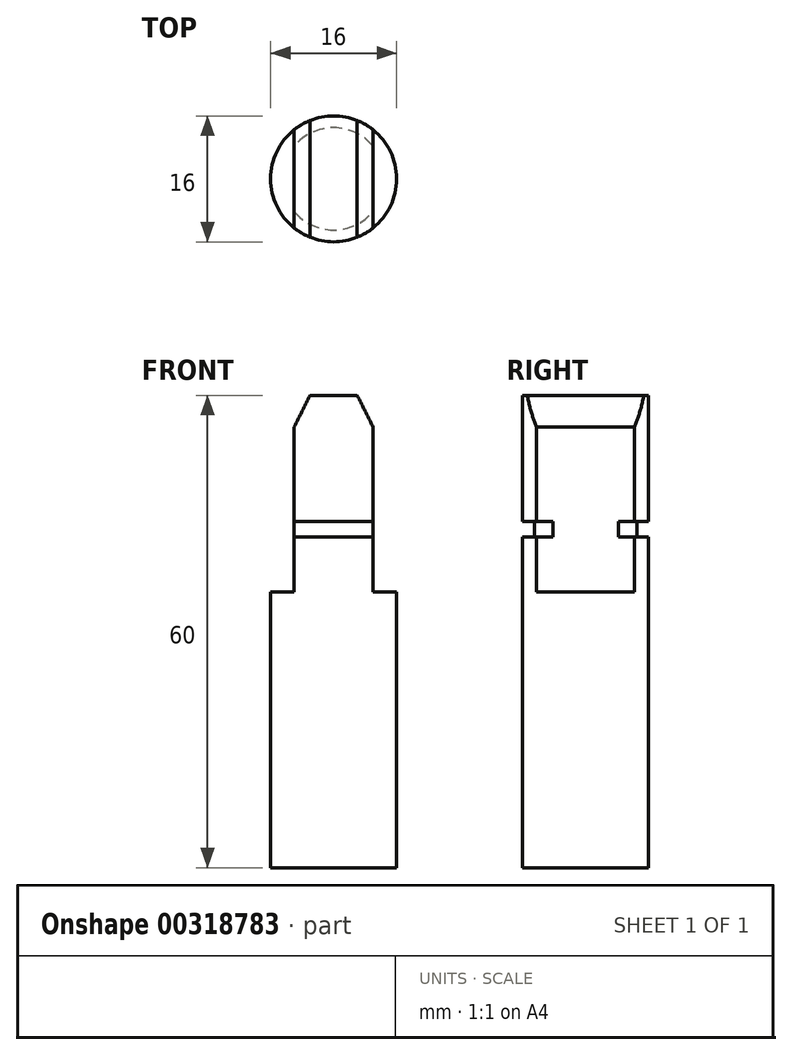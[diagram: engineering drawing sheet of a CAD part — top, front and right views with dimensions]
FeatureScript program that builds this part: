
annotation { "Feature Type Name" : "Feature", "Feature Type Description" : "" }
export const myFeature = defineFeature(function(context is Context, id is Id, definition is map)
    precondition{}
    {
        {
            var Q0;
            Q0=qCreatedBy(makeId("Top.planeOp"),FACE);
            var sketch = newSketch(context, id + "F0", { "sketchPlane" : qUnion([Q0])});
            skCircle(sketch, "E0", {"center": v(0, 0) * mm, "radius": 8 * mm});
            skSolve(sketch);
        }
        {
            var Q0;
            Q0=makeQuery(id+"F0.imprint","IMPRINT",FACE,{"disambiguationData":[TD([[makeQuery(id+"F0.imprint","IMPRINT",EDGE,{"derivedFrom":sQuery(id+"F0.wireOp",EDGE,"E0")}),1.0]])]});
            extrude(context, id + "F1", {"entities" : qUnion([Q0]), "depth" : 35 * mm, "symmetric" : true});
        }
        {
            var Q0;
            Q0=makeQuery(id+"F1.opExtrude","CAP_FACE",FACE,{"disambiguationData":[OSD([sQuery(id+"F0.wireOp",EDGE,"E0")])],"isStart":false});
            var sketch = newSketch(context, id + "F2", { "sketchPlane" : qUnion([Q0])});
            skLineSegment(sketch, "E1", {"start": v(-5, 6.24) * mm, "end": v(-5, -6.24) * mm});
            skLineSegment(sketch, "E2.MirrorCS", {"start": v(5, 6.24) * mm, "end": v(5, -6.24) * mm});
            skArc(sketch, "E3", {"start": v(5, 6.24) * mm, "mid": v(0, 11.24) * mm, "end": v(-5, 6.24) * mm});
            skArc(sketch, "E4.MirrorCS", {"start": v(5, -6.24) * mm, "mid": v(0, -11.24) * mm, "end": v(-5, -6.24) * mm});
            skSolve(sketch);
        }
        {
            var Q0;
            Q0=makeQuery(id+"F2.imprint","IMPRINT",FACE,{"disambiguationData":[TD([[makeQuery(id+"F2.imprint","IMPRINT",EDGE,{"derivedFrom":sQuery(id+"F2.wireOp",EDGE,"E1")}),1.0]])]});
            extrude(context, id + "F3", {"entities" : qUnion([Q0]), "operationType" : NewBodyOperationType.ADD, "depth" : 25 * mm});
        }
        {
            var Q0;
            Q0=makeQuery(id+"F3.opExtrude","CAP_EDGE",EDGE,{"disambiguationData":[OSD([sQuery(id+"F2.wireOp",EDGE,"E1")])],"isStart":false});
            var Q1;
            Q1=makeQuery(id+"F3.opExtrude","CAP_EDGE",EDGE,{"disambiguationData":[OSD([sQuery(id+"F2.wireOp",EDGE,"E2.MirrorCS")])],"isStart":false});
            chamfer(context, id + "F4", {"entities" : qUnion([Q0, Q1]), "chamferType" : ChamferType.TWO_OFFSETS, "width1" : 2 * mm, "oppositeDirection" : false, "width2" : 4 * mm, "tangentPropagation" : true});
        }
        {
            var Q0;
            Q0=qCreatedBy(makeId("Top.planeOp"),FACE);
            cPlane(context, id + "F5", {"entities" : qUnion([Q0]), "cplaneType" : CPlaneType.OFFSET, "offset" : 26.5 * mm, "width" : 150 * mm, "height" : 150 * mm});
        }
        {
            var Q0;
            Q0=qCreatedBy(id+"F5.planeOp",FACE);
            var sketch = newSketch(context, id + "F6", { "sketchPlane" : qUnion([Q0])});
            skCircle(sketch, "E5", {"center": v(0, 0) * mm, "radius": 8 * mm});
            skCircle(sketch, "E6", {"center": v(0, 0) * mm, "radius": 6.5 * mm});
            skSolve(sketch);
        }
        {
            var Q0;
            Q0=makeQuery(id+"F6.imprint","IMPRINT",FACE,{"disambiguationData":[TD([[makeQuery(id+"F6.imprint","IMPRINT",EDGE,{"derivedFrom":sQuery(id+"F6.wireOp",EDGE,"E5")}),1.0]])]});
            extrude(context, id + "F7", {"entities" : qUnion([Q0]), "operationType" : NewBodyOperationType.REMOVE, "oppositeDirection" : true, "depth" : 2 * mm});
        }
    });
